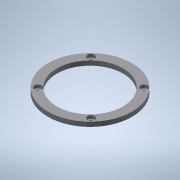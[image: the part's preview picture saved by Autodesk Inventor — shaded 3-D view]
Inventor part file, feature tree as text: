
AUTODESK INVENTOR PART (.ipt)
format: ipt  version: 2021 (Build 250183000, 183)  size: 117,248 bytes
history: native  units: in
note: dims shown in document units (in); Inventor stores cm internally (conversion verified against a paired STEP export)
features: sketch x2, extrude x1, hole x1
ambient origin geometry x8: Origin, YZ Plane, XZ Plane, XY Plane, X Axis, Y Axis, Z Axis, Center Point
bodies: Solid1 (feature_tree)
feature tree (4):
  extrude  "Extrusion1"  Depth=2.2047in
  hole  "Hole3"  [1 undecoded]
  sketch  "Sketch1"  dims[d0=1.7323in d1=2.2047in]
  sketch  "Sketch5"  dims[d2=0.1181in d3=0.0in d22=1.3917in d23=1.3917in d24=0.096in d25=0.2362in d26=0.1875in d27=0.086in d28=90.0deg d29=0.315in d30=0.8108in]
note: 1 required parameter value undecoded (feature->parameter linkage not recoverable at this tier; creation-order binding heuristic only, values carry confidence <= 0.55)
